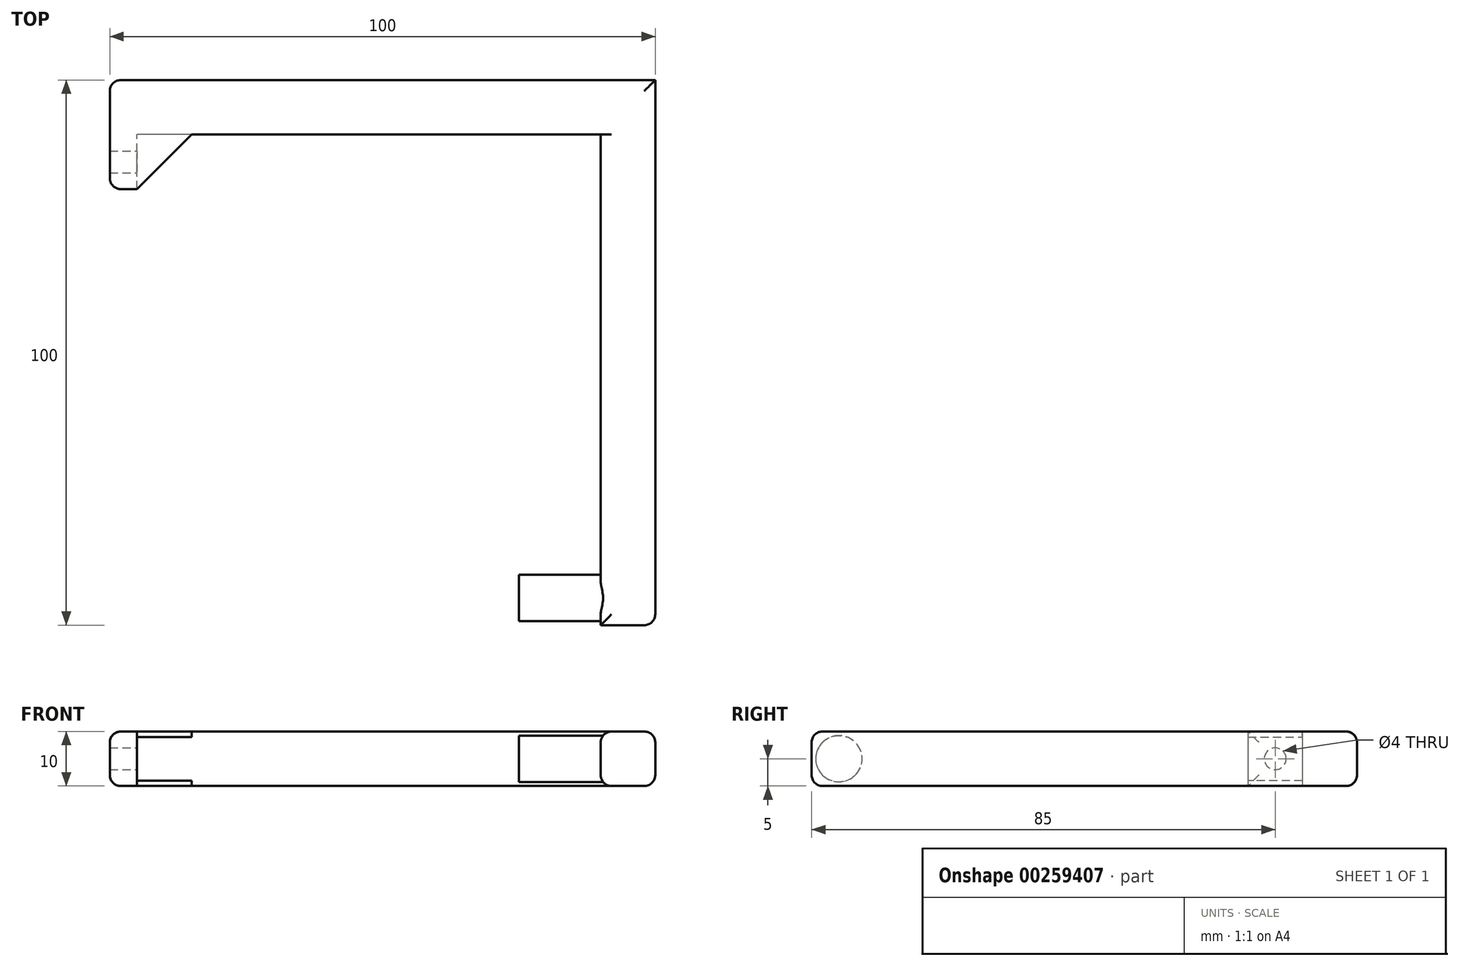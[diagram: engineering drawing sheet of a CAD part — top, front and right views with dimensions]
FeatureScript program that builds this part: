
annotation { "Feature Type Name" : "Feature", "Feature Type Description" : "" }
export const myFeature = defineFeature(function(context is Context, id is Id, definition is map)
    precondition{}
    {
        {
            var Q0;
            Q0=qCreatedBy(makeId("Top.planeOp"),FACE);
            var sketch = newSketch(context, id + "F0", { "sketchPlane" : qUnion([Q0])});
            skLineSegment(sketch, "E0.bottom", {"start": v(0, 0) * mm, "end": v(10, 0) * mm});
            skLineSegment(sketch, "E0.top", {"start": v(0, 100) * mm, "end": v(10, 100) * mm});
            skLineSegment(sketch, "E0.left", {"start": v(0, 0) * mm, "end": v(0, 90) * mm});
            skLineSegment(sketch, "E0.right", {"start": v(10, 0) * mm, "end": v(10, 100) * mm});
            skLineSegment(sketch, "E1.bottom", {"start": v(0, 100) * mm, "end": v(-90, 100) * mm});
            skLineSegment(sketch, "E1.top", {"start": v(0, 90) * mm, "end": v(-90, 90) * mm});
            skLineSegment(sketch, "E1.right", {"start": v(-90, 100) * mm, "end": v(-90, 90) * mm});
            skSolve(sketch);
        }
        {
            var Q0;
            Q0 = qSketchRegion(id + "F0", true);
            extrude(context, id + "F1", {"entities" : qUnion([Q0]), "depth" : 10 * mm});
        }
        {
            var Q0;
            Q0=makeQuery(id+"F1.opExtrude","SWEPT_FACE",FACE,{"disambiguationData":[OSD([sQuery(id+"F0.wireOp",EDGE,"E0.left")])]});
            var sketch = newSketch(context, id + "F2", { "sketchPlane" : qUnion([Q0])});
            skCircle(sketch, "E2", {"center": v(-5, 5) * mm, "radius": 4.25 * mm});
            skSolve(sketch);
        }
        {
            var Q0;
            Q0 = qSketchRegion(id + "F2", true);
            extrude(context, id + "F3", {"entities" : qUnion([Q0]), "operationType" : NewBodyOperationType.ADD, "depth" : 15 * mm});
        }
        {
            var Q0;
            Q0=makeQuery(id+"F1.opExtrude","SWEPT_FACE",FACE,{"disambiguationData":[OSD([sQuery(id+"F0.wireOp",EDGE,"E1.top")])]});
            var sketch = newSketch(context, id + "F4", { "sketchPlane" : qUnion([Q0])});
            skLineSegment(sketch, "E3.bottom", {"start": v(-90, 10) * mm, "end": v(-85, 10) * mm});
            skLineSegment(sketch, "E3.top", {"start": v(-90, 0) * mm, "end": v(-85, 0) * mm});
            skLineSegment(sketch, "E3.left", {"start": v(-90, 10) * mm, "end": v(-90, 0) * mm});
            skLineSegment(sketch, "E3.right", {"start": v(-85, 10) * mm, "end": v(-85, 0) * mm});
            skSolve(sketch);
        }
        {
            var Q0;
            Q0 = qSketchRegion(id + "F4", true);
            extrude(context, id + "F5", {"entities" : qUnion([Q0]), "operationType" : NewBodyOperationType.ADD, "depth" : 10 * mm});
        }
        {
            var Q0;
            Q0=makeQuery(id+"F5.opExtrude","SWEPT_FACE",FACE,{"disambiguationData":[OSD([sQuery(id+"F4.wireOp",EDGE,"E3.right")])]});
            var sketch = newSketch(context, id + "F6", { "sketchPlane" : qUnion([Q0])});
            skCircle(sketch, "E4", {"center": v(85, 5) * mm, "radius": 2 * mm});
            skSolve(sketch);
        }
        {
            var Q0;
            Q0 = qSketchRegion(id + "F6", true);
            extrude(context, id + "F7", {"entities" : qUnion([Q0]), "operationType" : NewBodyOperationType.REMOVE, "oppositeDirection" : true, "depth" : 25.4 * mm});
        }
        {
            var Q0;
            Q0=makeQuery(id+"F5.boolean.opBoolean","MERGE",FACE,{"derivedFrom":[makeQuery(id+"F1.opExtrude","CAP_FACE",FACE,{"disambiguationData":[OSD([sQuery(id+"F0.wireOp",EDGE,"E0.bottom"),sQuery(id+"F0.wireOp",EDGE,"E0.top"),sQuery(id+"F0.wireOp",EDGE,"E0.left"),sQuery(id+"F0.wireOp",EDGE,"E0.right"),sQuery(id+"F0.wireOp",EDGE,"E1.bottom"),sQuery(id+"F0.wireOp",EDGE,"E1.top"),sQuery(id+"F0.wireOp",EDGE,"E1.right")])],"isStart":false}),makeQuery(id+"F5.opExtrude","SWEPT_FACE",FACE,{"disambiguationData":[OSD([sQuery(id+"F4.wireOp",EDGE,"E3.bottom")])]})]});
            var sketch = newSketch(context, id + "F8", { "sketchPlane" : qUnion([Q0])});
            skLineSegment(sketch, "E5", {"start": v(-85, 80) * mm, "end": v(-85, 90) * mm});
            skLineSegment(sketch, "E6", {"start": v(-85, 90) * mm, "end": v(-75, 90) * mm});
            skLineSegment(sketch, "E7", {"start": v(-75, 90) * mm, "end": v(-85, 80) * mm});
            skSolve(sketch);
        }
        {
            var Q0;
            Q0 = qSketchRegion(id + "F8", true);
            extrude(context, id + "F9", {"entities" : qUnion([Q0]), "operationType" : NewBodyOperationType.ADD, "oppositeDirection" : true, "depth" : 1 * mm});
        }
        {
            var Q0;
            Q0=makeQuery(id+"F5.boolean.opBoolean","MERGE",FACE,{"derivedFrom":[makeQuery(id+"F1.opExtrude","CAP_FACE",FACE,{"disambiguationData":[OSD([sQuery(id+"F0.wireOp",EDGE,"E0.bottom"),sQuery(id+"F0.wireOp",EDGE,"E0.top"),sQuery(id+"F0.wireOp",EDGE,"E0.left"),sQuery(id+"F0.wireOp",EDGE,"E0.right"),sQuery(id+"F0.wireOp",EDGE,"E1.bottom"),sQuery(id+"F0.wireOp",EDGE,"E1.top"),sQuery(id+"F0.wireOp",EDGE,"E1.right")])],"isStart":true}),makeQuery(id+"F5.opExtrude","SWEPT_FACE",FACE,{"disambiguationData":[OSD([sQuery(id+"F4.wireOp",EDGE,"E3.top")])]})]});
            var sketch = newSketch(context, id + "F10", { "sketchPlane" : qUnion([Q0])});
            skLineSegment(sketch, "E8", {"start": v(-85, -80) * mm, "end": v(-85, -90) * mm});
            skLineSegment(sketch, "E9", {"start": v(-85, -90) * mm, "end": v(-75, -90) * mm});
            skLineSegment(sketch, "E10", {"start": v(-75, -90) * mm, "end": v(-85, -80) * mm});
            skSolve(sketch);
        }
        {
            var Q0;
            Q0 = qSketchRegion(id + "F10", true);
            extrude(context, id + "F11", {"entities" : qUnion([Q0]), "oppositeDirection" : true, "depth" : 1 * mm});
        }
        {
            var Q0;
            Q0=makeQuery(id+"F1.opExtrude","CAP_EDGE",EDGE,{"disambiguationData":[OSD([sQuery(id+"F0.wireOp",EDGE,"E0.top"),sQuery(id+"F0.wireOp",EDGE,"E1.bottom")])],"isStart":true});
            var Q1;
            Q1=makeQuery(id+"F1.opExtrude","CAP_EDGE",EDGE,{"disambiguationData":[OSD([sQuery(id+"F0.wireOp",EDGE,"E0.top"),sQuery(id+"F0.wireOp",EDGE,"E1.bottom")])],"isStart":false});
            var Q2;
            Q2=makeQuery(id+"F5.boolean.opBoolean","MERGE",EDGE,{"derivedFrom":[makeQuery(id+"F1.opExtrude","CAP_EDGE",EDGE,{"disambiguationData":[OSD([sQuery(id+"F0.wireOp",EDGE,"E1.right")])],"isStart":false}),makeQuery(id+"F5.opExtrude","SWEPT_EDGE",EDGE,{"disambiguationData":[OSD([sQuery(id+"F4.wireOp",EDGE,"E3.bottom"),sQuery(id+"F4.wireOp",EDGE,"E3.left")])]})]});
            var Q3;
            Q3=makeQuery(id+"F5.boolean.opBoolean","MERGE",EDGE,{"derivedFrom":[makeQuery(id+"F1.opExtrude","CAP_EDGE",EDGE,{"disambiguationData":[OSD([sQuery(id+"F0.wireOp",EDGE,"E1.right")])],"isStart":true}),makeQuery(id+"F5.opExtrude","SWEPT_EDGE",EDGE,{"disambiguationData":[OSD([sQuery(id+"F4.wireOp",EDGE,"E3.top"),sQuery(id+"F4.wireOp",EDGE,"E3.left")])]})]});
            var Q4;
            Q4=makeQuery(id+"F5.opExtrude","CAP_EDGE",EDGE,{"disambiguationData":[OSD([sQuery(id+"F4.wireOp",EDGE,"E3.left")])],"isStart":false});
            var Q5;
            Q5=makeQuery(id+"F1.opExtrude","SWEPT_EDGE",EDGE,{"disambiguationData":[OSD([sQuery(id+"F0.wireOp",EDGE,"E1.bottom"),sQuery(id+"F0.wireOp",EDGE,"E1.right")])]});
            var Q6;
            Q6=makeQuery(id+"F1.opExtrude","CAP_EDGE",EDGE,{"disambiguationData":[OSD([sQuery(id+"F0.wireOp",EDGE,"E0.left")])],"isStart":false});
            var Q7;
            Q7=makeQuery(id+"F1.opExtrude","CAP_EDGE",EDGE,{"disambiguationData":[OSD([sQuery(id+"F0.wireOp",EDGE,"E0.right")])],"isStart":false});
            var Q8;
            Q8=makeQuery(id+"F1.opExtrude","CAP_EDGE",EDGE,{"disambiguationData":[OSD([sQuery(id+"F0.wireOp",EDGE,"E0.left")])],"isStart":true});
            var Q9;
            Q9=makeQuery(id+"F1.opExtrude","CAP_EDGE",EDGE,{"disambiguationData":[OSD([sQuery(id+"F0.wireOp",EDGE,"E0.right")])],"isStart":true});
            var Q10;
            Q10=makeQuery(id+"F1.opExtrude","SWEPT_EDGE",EDGE,{"disambiguationData":[OSD([sQuery(id+"F0.wireOp",EDGE,"E0.bottom"),sQuery(id+"F0.wireOp",EDGE,"E0.right")])]});
            var Q11;
            Q11=makeQuery(id+"F1.opExtrude","CAP_EDGE",EDGE,{"disambiguationData":[OSD([sQuery(id+"F0.wireOp",EDGE,"E0.bottom")])],"isStart":false});
            var Q12;
            Q12=makeQuery(id+"F1.opExtrude","CAP_EDGE",EDGE,{"disambiguationData":[OSD([sQuery(id+"F0.wireOp",EDGE,"E0.bottom")])],"isStart":true});
            fillet(context, id + "F12", {"entities" : qUnion([Q0, Q1, Q2, Q3, Q4, Q5, Q6, Q7, Q8, Q9, Q10, Q11, Q12]), "radius" : 2 * mm, "tangentPropagation" : true, "allowEdgeOverflow" : false});
        }
    });
